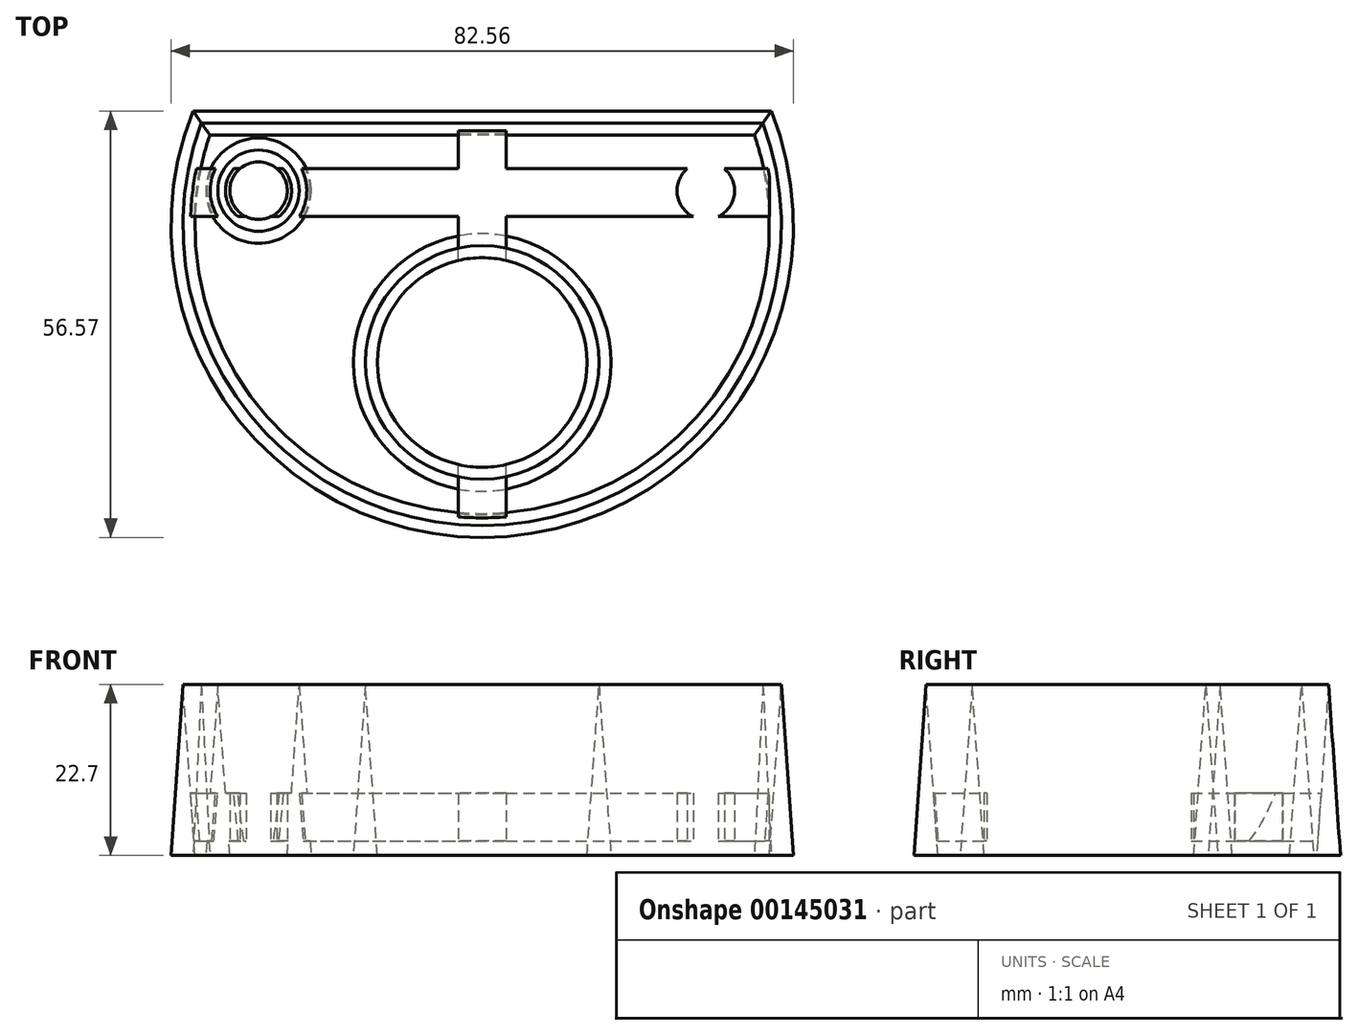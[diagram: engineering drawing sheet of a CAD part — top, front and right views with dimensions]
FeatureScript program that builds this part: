
annotation { "Feature Type Name" : "Feature", "Feature Type Description" : "" }
export const myFeature = defineFeature(function(context is Context, id is Id, definition is map)
    precondition{}
    {
        {
            var Q0;
            Q0=qCreatedBy(makeId("Top.planeOp"),FACE);
            var sketch = newSketch(context, id + "F0", { "sketchPlane" : qUnion([Q0])});
            skArc(sketch, "E0", {"start": v(-36.12, 12.12) * mm, "mid": v(0, -38.1) * mm, "end": v(36.12, 12.12) * mm});
            skLineSegment(sketch, "E1", {"start": v(-36.12, 12.12) * mm, "end": v(36.12, 12.12) * mm});
            skLineSegment(sketch, "E2", {"start": v(0, 12.12) * mm, "end": v(0, -38.1) * mm, "construction": true});
            skCircle(sketch, "E3", {"center": v(0, -18.07) * mm, "radius": 13.9 * mm});
            skLineSegment(sketch, "E4", {"start": v(-44.12, 4.72) * mm, "end": v(51.54, 4.72) * mm, "construction": true});
            skCircle(sketch, "E5", {"center": v(-29.66, 4.72) * mm, "radius": 3.81 * mm});
            skArc(sketch, "E6.0", {"start": v(-38.34, 15.3) * mm, "mid": v(0, -41.27) * mm, "end": v(38.34, 15.3) * mm});
            skLineSegment(sketch, "E6.1", {"start": v(-38.34, 15.3) * mm, "end": v(38.34, 15.3) * mm});
            skCircle(sketch, "E7.0", {"center": v(0, -18.07) * mm, "radius": 17.08 * mm});
            skCircle(sketch, "E8.0", {"center": v(-29.66, 4.72) * mm, "radius": 6.99 * mm});
            skCircle(sketch, "E9.MirrorC", {"center": v(29.66, 4.72) * mm, "radius": 3.81 * mm});
            skCircle(sketch, "E10.MirrorC", {"center": v(29.66, 4.72) * mm, "radius": 6.99 * mm});
            skSolve(sketch);
        }
        {
            var Q0;
            Q0=makeQuery(id+"F0.imprint","IMPRINT",FACE,{"disambiguationData":[TD([[makeQuery(id+"F0.imprint","IMPRINT",EDGE,{"derivedFrom":sQuery(id+"F0.wireOp",EDGE,"E0")}),-1.0]])]});
            var Q1;
            Q1=makeQuery(id+"F0.imprint","IMPRINT",FACE,{"disambiguationData":[TD([[makeQuery(id+"F0.imprint","IMPRINT",EDGE,{"derivedFrom":sQuery(id+"F0.wireOp",EDGE,"E5")}),-1.0]])]});
            var Q2;
            Q2=makeQuery(id+"F0.imprint","IMPRINT",FACE,{"disambiguationData":[TD([[makeQuery(id+"F0.imprint","IMPRINT",EDGE,{"derivedFrom":sQuery(id+"F0.wireOp",EDGE,"E9.MirrorC")}),1.0]])]});
            var Q3;
            Q3=makeQuery(id+"F0.imprint","IMPRINT",FACE,{"disambiguationData":[TD([[makeQuery(id+"F0.imprint","IMPRINT",EDGE,{"derivedFrom":sQuery(id+"F0.wireOp",EDGE,"E3")}),-1.0]])]});
            extrude(context, id + "F1", {"entities" : qUnion([Q0, Q1, Q2, Q3]), "depth" : 25.4 * mm, "hasDraft" : true, "draftAngle" : 4 * degree, "draftPullDirection" : true});
        }
        {
            var Q0;
            Q0=qCreatedBy(makeId("Front.planeOp"),FACE);
            cPlane(context, id + "F2", {"entities" : qUnion([Q0]), "cplaneType" : CPlaneType.OFFSET, "offset" : 13.72 * mm, "oppositeDirection" : true, "width" : 152.4 * mm, "height" : 152.4 * mm});
        }
        {
            var Q0;
            Q0=qCreatedBy(id+"F2.planeOp",FACE);
            var sketch = newSketch(context, id + "F3", { "sketchPlane" : qUnion([Q0])});
            skLineSegment(sketch, "E11", {"start": v(0, 0) * mm, "end": v(0, 18.97) * mm, "construction": true});
            skLineSegment(sketch, "E12.bottom", {"start": v(-3.17, 1.9) * mm, "end": v(3.18, 1.9) * mm});
            skLineSegment(sketch, "E12.top", {"start": v(-3.18, 8.26) * mm, "end": v(3.18, 8.26) * mm});
            skLineSegment(sketch, "E12.left", {"start": v(-3.17, 1.9) * mm, "end": v(-3.18, 8.26) * mm});
            skLineSegment(sketch, "E12.right", {"start": v(3.18, 1.9) * mm, "end": v(3.17, 8.26) * mm});
            skPoint(sketch, "E12.middle", {"position": v(0, 5.08) * mm});
            skSolve(sketch);
        }
        {
            var Q0;
            Q0 = qSketchRegion(id + "F5", true);
            var Q1;
            Q1 = qSketchRegion(id + "F3", true);
            var Q2;
            Q2=makeQuery(id+"F1.opExtrude","SWEPT_FACE",FACE,{"disambiguationData":[OSD([sQuery(id+"F0.wireOp",EDGE,"E0")])]});
            extrude(context, id + "F4", {"entities" : qUnion([Q0, Q1]), "endBound" : BoundingType.UP_TO_SURFACE, "endBoundEntityFace" : qUnion([Q2]), "depth" : 25.4 * mm});
        }
        {
            var Q0;
            Q0=makeQuery(id+"F1.opExtrude","CAP_FACE",FACE,{"disambiguationData":[OSD([sQuery(id+"F0.wireOp",EDGE,"E3"),sQuery(id+"F0.wireOp",EDGE,"E7.0")])],"isStart":true});
            var sketch = newSketch(context, id + "F5", { "sketchPlane" : qUnion([Q0])});
            skCircle(sketch, "E13.0", {"center": v(0, 18.07) * mm, "radius": 13.9 * mm});
            skSolve(sketch);
        }
        {
            var Q0;
            Q0 = qSketchRegion(id + "F5", true);
            extrude(context, id + "F6", {"entities" : qUnion([Q0]), "operationType" : NewBodyOperationType.REMOVE, "oppositeDirection" : true, "depth" : 60.53 * mm});
        }
        {
            var Q0;
            Q0=qCreatedBy(makeId("Right.planeOp"),FACE);
            cPlane(context, id + "F7", {"entities" : qUnion([Q0]), "cplaneType" : CPlaneType.OFFSET, "offset" : 38.1 * mm, "width" : 152.4 * mm, "height" : 152.4 * mm});
        }
        {
            var Q0;
            Q0=qCreatedBy(id+"F7.planeOp",FACE);
            var sketch = newSketch(context, id + "F8", { "sketchPlane" : qUnion([Q0])});
            skLineSegment(sketch, "E14", {"start": v(4.46, 0) * mm, "end": v(4.46, 26.46) * mm, "construction": true});
            skLineSegment(sketch, "E15.bottom", {"start": v(7.64, 1.9) * mm, "end": v(1.29, 1.9) * mm});
            skLineSegment(sketch, "E15.top", {"start": v(7.64, 8.26) * mm, "end": v(1.29, 8.26) * mm});
            skLineSegment(sketch, "E15.left", {"start": v(7.64, 1.9) * mm, "end": v(7.64, 8.25) * mm});
            skLineSegment(sketch, "E15.right", {"start": v(1.29, 1.9) * mm, "end": v(1.29, 8.26) * mm});
            skPoint(sketch, "E15.middle", {"position": v(4.46, 5.08) * mm});
            skSolve(sketch);
        }
        {
            var Q0;
            Q0 = qSketchRegion(id + "F8", true);
            var Q1;
            Q1=makeQuery(id+"F1.opExtrude","SWEPT_FACE",FACE,{"disambiguationData":[OSD([sQuery(id+"F0.wireOp",EDGE,"E0")])]});
            var Q2;
            Q2=makeQuery(id+"F1.opExtrude","SWEPT_BODY",BODY,{"disambiguationData":[OSD([sQuery(id+"F0.wireOp",EDGE,"E0"),sQuery(id+"F0.wireOp",EDGE,"E1"),sQuery(id+"F0.wireOp",EDGE,"E6.0"),sQuery(id+"F0.wireOp",EDGE,"E6.1")])]});
            extrude(context, id + "F9", {"entities" : qUnion([Q0]), "operationType" : NewBodyOperationType.ADD, "oppositeDirection" : true, "endBoundEntityFace" : qUnion([Q1]), "endBoundEntityBody" : qUnion([Q2]), "depth" : 77.72 * mm});
        }
        {
            var Q0;
            Q0=makeQuery(id+"F1.opExtrude","CAP_FACE",FACE,{"disambiguationData":[OSD([sQuery(id+"F0.wireOp",EDGE,"E0"),sQuery(id+"F0.wireOp",EDGE,"E1"),sQuery(id+"F0.wireOp",EDGE,"E6.0"),sQuery(id+"F0.wireOp",EDGE,"E6.1")])],"isStart":true});
            var sketch = newSketch(context, id + "F10", { "sketchPlane" : qUnion([Q0])});
            skCircle(sketch, "E16.0", {"center": v(-29.66, -4.72) * mm, "radius": 3.81 * mm});
            skCircle(sketch, "E16.1", {"center": v(29.66, -4.72) * mm, "radius": 3.81 * mm});
            skSolve(sketch);
        }
        {
            var Q0;
            Q0 = qSketchRegion(id + "F10", true);
            extrude(context, id + "F11", {"entities" : qUnion([Q0]), "operationType" : NewBodyOperationType.REMOVE, "oppositeDirection" : true, "depth" : 35.63 * mm});
        }
    });
